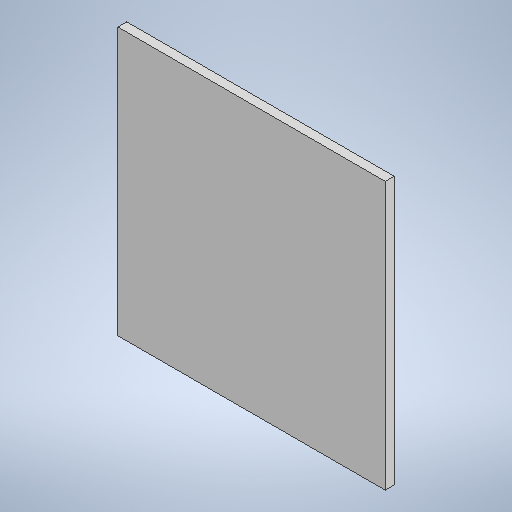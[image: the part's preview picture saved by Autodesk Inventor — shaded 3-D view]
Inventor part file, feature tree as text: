
AUTODESK INVENTOR PART (.ipt)
format: ipt  version: 2025.1 (Build 291241020, 241B)  size: 226,816 bytes
history: native  units: in
note: dims shown in document units (in); Inventor stores cm internally (conversion verified against a paired STEP export)
features: extrude x1, sketch x1
ambient origin geometry x8: Origin, YZ Plane, XZ Plane, XY Plane, X Axis, Y Axis, Z Axis, Center Point
bodies: Solid1 (feature_tree)
feature tree (2):
  extrude  "Extrusion1"  [1 undecoded]
  sketch  "Sketch1"  dims[d27=0.2in d28=0.0in]
note: 1 required parameter value undecoded (feature->parameter linkage not recoverable at this tier; creation-order binding heuristic only, values carry confidence <= 0.55)
